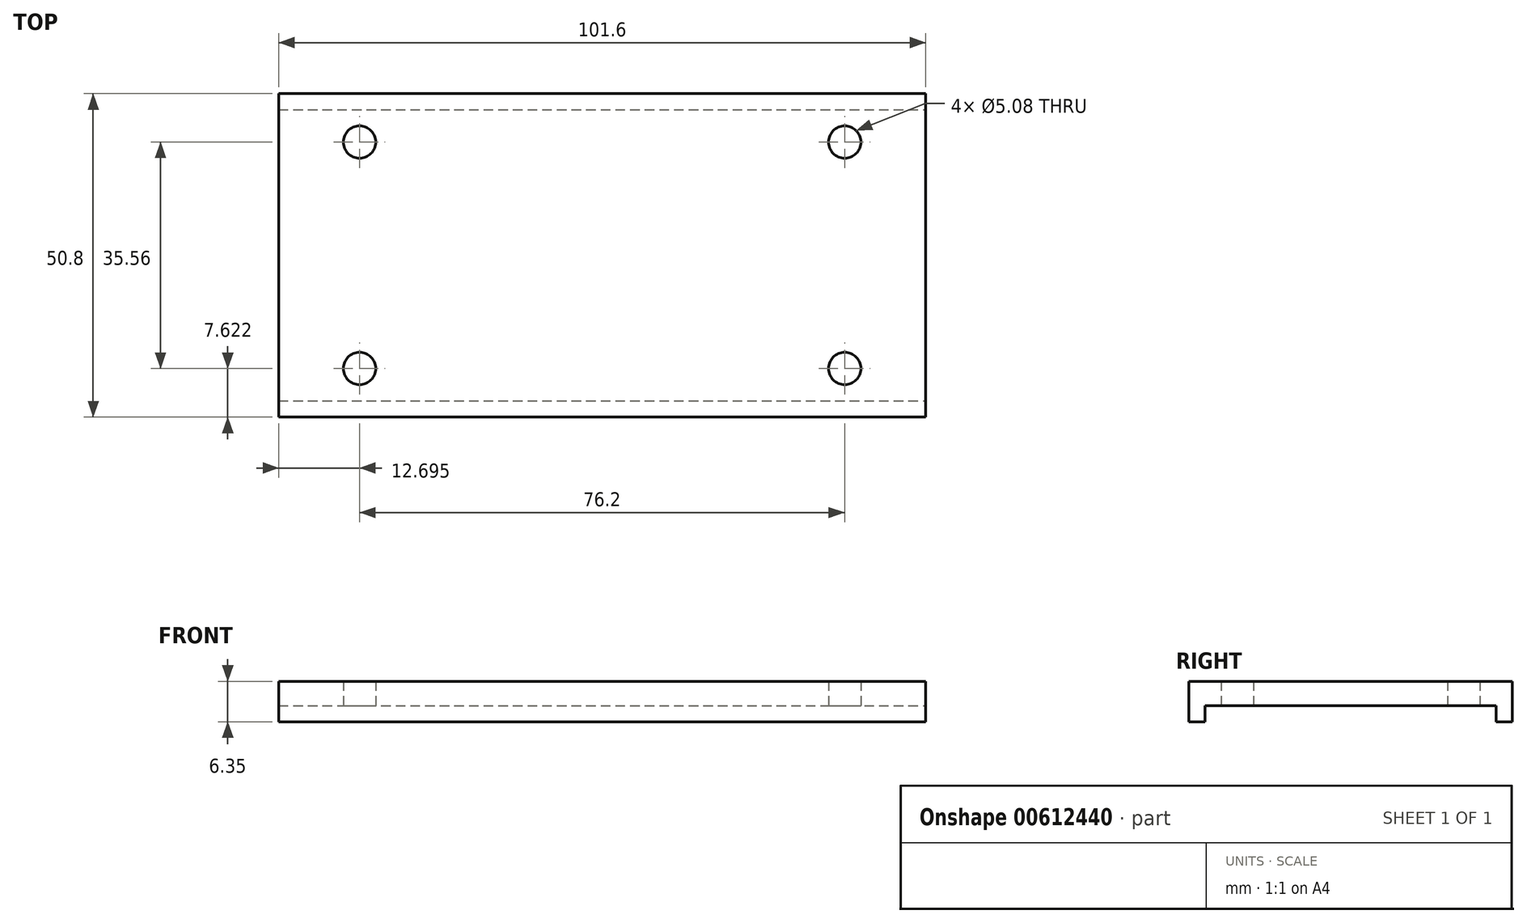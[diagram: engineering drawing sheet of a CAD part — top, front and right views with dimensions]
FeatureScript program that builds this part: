
annotation { "Feature Type Name" : "Feature", "Feature Type Description" : "" }
export const myFeature = defineFeature(function(context is Context, id is Id, definition is map)
    precondition{}
    {
        {
            var Q0;
            Q0=qCreatedBy(makeId("Top.planeOp"),FACE);
            var sketch = newSketch(context, id + "F0", { "sketchPlane" : qUnion([Q0])});
            skLineSegment(sketch, "E0.bottom", {"start": v(-52.12, -26.7) * mm, "end": v(49.48, -26.7) * mm});
            skLineSegment(sketch, "E0.top", {"start": v(-52.12, 24.1) * mm, "end": v(49.48, 24.1) * mm});
            skLineSegment(sketch, "E0.left", {"start": v(-52.12, -26.7) * mm, "end": v(-52.12, 24.1) * mm});
            skLineSegment(sketch, "E0.right", {"start": v(49.48, -26.7) * mm, "end": v(49.48, 24.1) * mm});
            skSolve(sketch);
        }
        {
            var Q0;
            Q0 = qSketchRegion(id + "F0", true);
            extrude(context, id + "F1", {"entities" : qUnion([Q0]), "oppositeDirection" : true, "depth" : 3.8 * mm, "offsetDistance" : 25.4 * mm});
        }
        {
            var Q0;
            Q0=makeQuery(id+"F1.opExtrude","CAP_FACE",FACE,{"disambiguationData":[OSD([sQuery(id+"F0.wireOp",EDGE,"E0.bottom"),sQuery(id+"F0.wireOp",EDGE,"E0.top"),sQuery(id+"F0.wireOp",EDGE,"E0.left"),sQuery(id+"F0.wireOp",EDGE,"E0.right")])],"isStart":false});
            var sketch = newSketch(context, id + "F2", { "sketchPlane" : qUnion([Q0])});
            skLineSegment(sketch, "E1.bottom", {"start": v(-52.12, 26.7) * mm, "end": v(49.48, 26.7) * mm});
            skLineSegment(sketch, "E1.top", {"start": v(-52.12, 24.16) * mm, "end": v(49.48, 24.16) * mm});
            skLineSegment(sketch, "E1.left", {"start": v(-52.12, 26.7) * mm, "end": v(-52.12, 24.16) * mm});
            skLineSegment(sketch, "E1.right", {"start": v(49.48, 26.7) * mm, "end": v(49.48, 24.16) * mm});
            skLineSegment(sketch, "E2.bottom", {"start": v(-52.12, -24.1) * mm, "end": v(49.48, -24.1) * mm});
            skLineSegment(sketch, "E2.top", {"start": v(-52.12, -21.56) * mm, "end": v(49.48, -21.56) * mm});
            skLineSegment(sketch, "E2.left", {"start": v(-52.12, -24.1) * mm, "end": v(-52.12, -21.56) * mm});
            skLineSegment(sketch, "E2.right", {"start": v(49.48, -24.1) * mm, "end": v(49.48, -21.56) * mm});
            skSolve(sketch);
        }
        {
            var Q0;
            Q0 = qSketchRegion(id + "F2", true);
            extrude(context, id + "F3", {"entities" : qUnion([Q0]), "operationType" : NewBodyOperationType.ADD, "depth" : 2.54 * mm, "offsetDistance" : 25.4 * mm});
        }
        {
            var Q0;
            Q0=makeQuery(id+"F1.opExtrude","CAP_FACE",FACE,{"disambiguationData":[OSD([sQuery(id+"F0.wireOp",EDGE,"E0.bottom"),sQuery(id+"F0.wireOp",EDGE,"E0.top"),sQuery(id+"F0.wireOp",EDGE,"E0.left"),sQuery(id+"F0.wireOp",EDGE,"E0.right")])],"isStart":false});
            var sketch = newSketch(context, id + "F4", { "sketchPlane" : qUnion([Q0])});
            skCircle(sketch, "E3", {"center": v(-39.42, 19.08) * mm, "radius": 2.54 * mm});
            skCircle(sketch, "E4", {"center": v(-39.42, -16.48) * mm, "radius": 2.54 * mm});
            skCircle(sketch, "E5", {"center": v(36.78, 19.08) * mm, "radius": 2.54 * mm});
            skCircle(sketch, "E6", {"center": v(36.78, -16.48) * mm, "radius": 2.54 * mm});
            skSolve(sketch);
        }
        {
            var Q0;
            Q0 = qSketchRegion(id + "F4", true);
            extrude(context, id + "F5", {"entities" : qUnion([Q0]), "operationType" : NewBodyOperationType.REMOVE, "oppositeDirection" : true, "depth" : 3.8 * mm, "offsetDistance" : 25.4 * mm});
        }
    });
